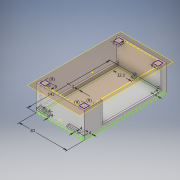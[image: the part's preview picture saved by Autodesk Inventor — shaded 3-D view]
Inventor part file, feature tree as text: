
AUTODESK INVENTOR PART (.ipt)
format: ipt  version: 2019.1 (Build 231200000, 200)  size: 271,872 bytes
history: native  units: in
note: dims shown in document units (in); Inventor stores cm internally (conversion verified against a paired STEP export)
features: extrude x13, other x5, sketch x4, hole x2, chamfer x1, plane x1
ambient origin geometry x8: Origin, YZ Plane, XZ Plane, XY Plane, X Axis, Y Axis, Z Axis, Center Point
bodies: Solid1 (feature_tree)
feature tree (26):
  sketch  "Sketch1"  dims[d0=5.6299in d1=3.2677in]
  extrude  "Floor"  Depth=3.2677in
  extrude  "Walls"  Depth=0.1181in TaperAngle=0.0deg
  sketch  "Sketch2"  dims[d2=0.1181in d20=0.1181in d21=0.0in]
  extrude  "mounts"  Depth=0.1575in
  hole  "Hole1"  [1 undecoded]
  extrude  "Extrusion5"  Depth=0.0295in
  extrude  "Extrusion6"  Depth=0.0295in
  extrude  "Extrusion7"  Depth=0.0295in
  extrude  "Extrusion8"  Depth=0.0295in
  extrude  "Extrusion9"  Depth=0.0295in
  chamfer  "Chamfer1"  Distance=0.315in
  other  "Work Point1"
  hole  "Hole2"  [1 undecoded]
  extrude  "Extrusion10"  Depth=0.0295in TaperAngle=0.0deg
  extrude  "Extrusion11"  Depth=0.315in TaperAngle=0.0deg
  extrude  "Extrusion12"  Depth=0.315in TaperAngle=0.0deg
  plane  "Work Plane1"
  sketch  "Sketch4"  dims[d31=0.1575in d32=0.1575in d33=0.1575in d34=0.1575in d35=0.1575in d36=0.1575in d37=1.2638in d42=0.315in d43=0.0in d44=0.1181in d45=0.2362in d46=0.1575in d47=0.0787in d48=90.0deg d49=0.315in d50=0.0in d51=0.7874in d52=0.0in d53=0.7874in d54=0.0in d55=0.315in d56=0.0in d57=0.315in d58=0.0in d59=0.2165in d60=0.1969in d62=0.1654in d63=0.0in d64=0.0492in d65=0.0787in d66=45.0deg d67=0.3937in d68=0.3937in d69=0.1575in d70=0.2362in d71=0.1772in d72=0.0394in d73=90.0deg d74=0.1969in d75=0.0in d76=1.7717in d77=0.0in d78=1.7717in d79=0.0in d80=0.3937in d81=0.3937in d82=1.7717in d83=0.0in d84=0.3543in d85=0.3543in d86=0.3543in d87=0.3543in d88=0.3543in d89=0.3543in d90=0.3543in d91=0.1969in d92=0.0in d93=0.1969in d94=0.0in d61=0.0394in d95=0.0394in d96=0.0394in d97=0.0394in d98=0.0059in d99=0.0098in d100=0.0148in d101=0.5635in d102=0.0295in d103=0.8108in d104=0.0025in d105=0.0295in d106=0.0148in]
  extrude  "Extrusion13"  Depth=0.2165in
  extrude  "Extrusion14"  Depth=0.1969in
  other  "Work Point3"
  other  "Work Point4"
  other  "Work Point5"
  other  "Work Point6"
  sketch  "Sketch3"  dims[d24=0.7874in d25=0.0in d30=0.1575in]
note: 2 required parameter values undecoded (feature->parameter linkage not recoverable at this tier; creation-order binding heuristic only, values carry confidence <= 0.55)
